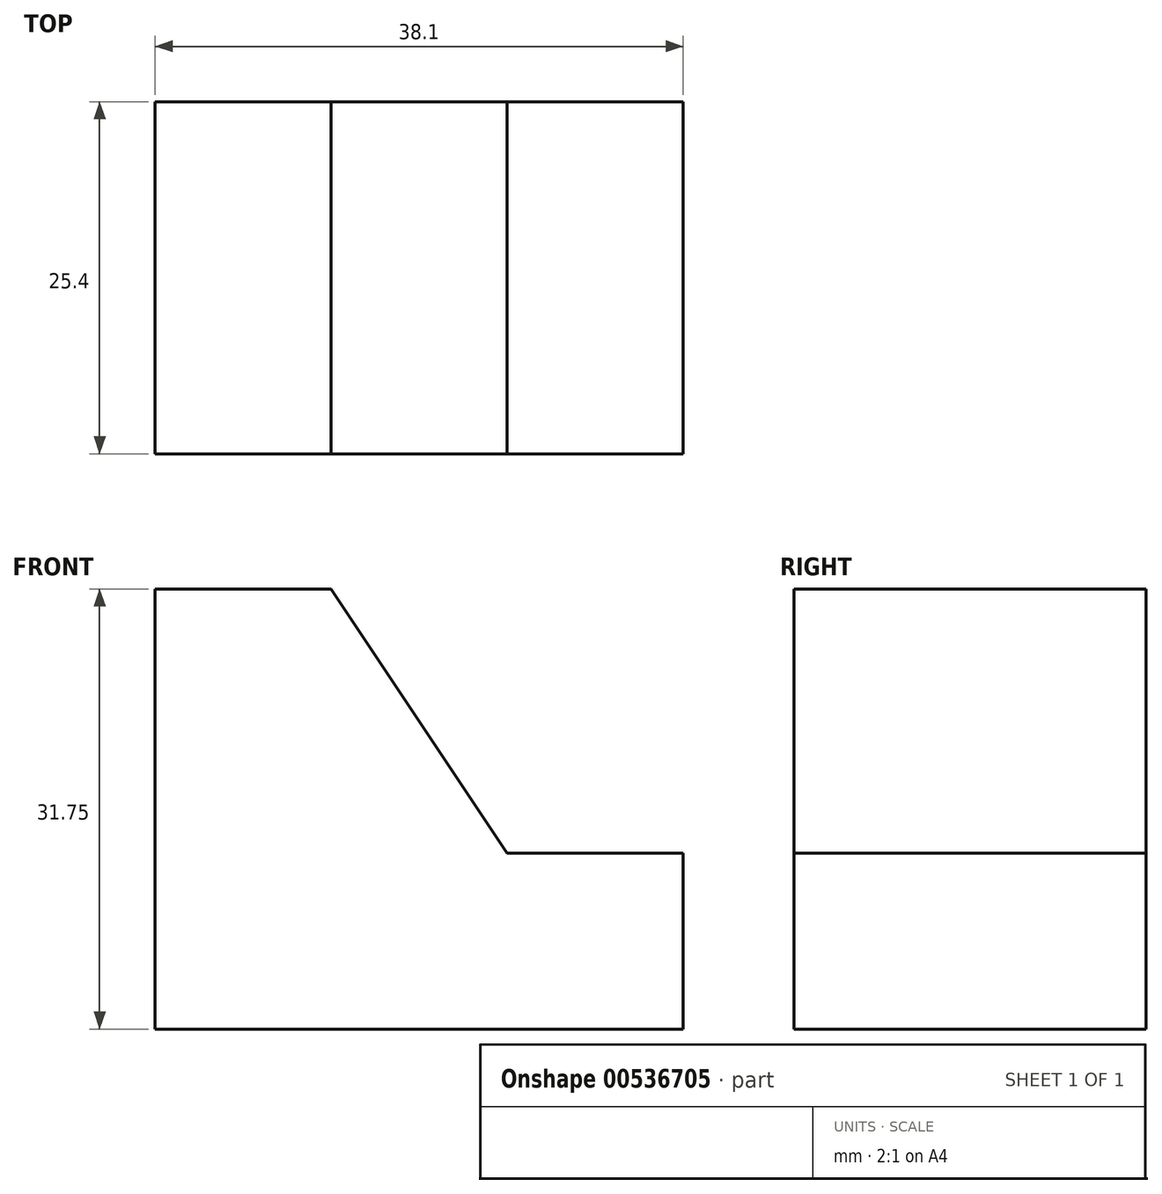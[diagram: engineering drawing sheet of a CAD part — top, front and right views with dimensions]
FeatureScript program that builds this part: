
annotation { "Feature Type Name" : "Feature", "Feature Type Description" : "" }
export const myFeature = defineFeature(function(context is Context, id is Id, definition is map)
    precondition{}
    {
        {
            var Q0;
            Q0=qCreatedBy(makeId("Front.planeOp"),FACE);
            var sketch = newSketch(context, id + "F0", { "sketchPlane" : qUnion([Q0])});
            skLineSegment(sketch, "E0", {"start": v(-23.78, 0) * mm, "end": v(-23.78, 31.75) * mm});
            skLineSegment(sketch, "E1", {"start": v(-23.78, 31.75) * mm, "end": v(-11.08, 31.75) * mm});
            skLineSegment(sketch, "E2", {"start": v(-23.78, 0) * mm, "end": v(14.32, 0) * mm});
            skLineSegment(sketch, "E3", {"start": v(14.32, 0) * mm, "end": v(14.32, 12.7) * mm});
            skLineSegment(sketch, "E4", {"start": v(14.32, 12.7) * mm, "end": v(1.62, 12.7) * mm});
            skLineSegment(sketch, "E5", {"start": v(1.62, 12.7) * mm, "end": v(-11.08, 31.75) * mm});
            skSolve(sketch);
        }
        {
            var Q0;
            Q0=makeQuery(id+"F0.imprint","IMPRINT",FACE,{"disambiguationData":[TD([[makeQuery(id+"F0.imprint","IMPRINT",EDGE,{"derivedFrom":sQuery(id+"F0.wireOp",EDGE,"E0")}),-1.0]])]});
            extrude(context, id + "F1", {"entities" : qUnion([Q0]), "depth" : 25.4 * mm, "offsetDistance" : 25.4 * mm});
        }
    });
